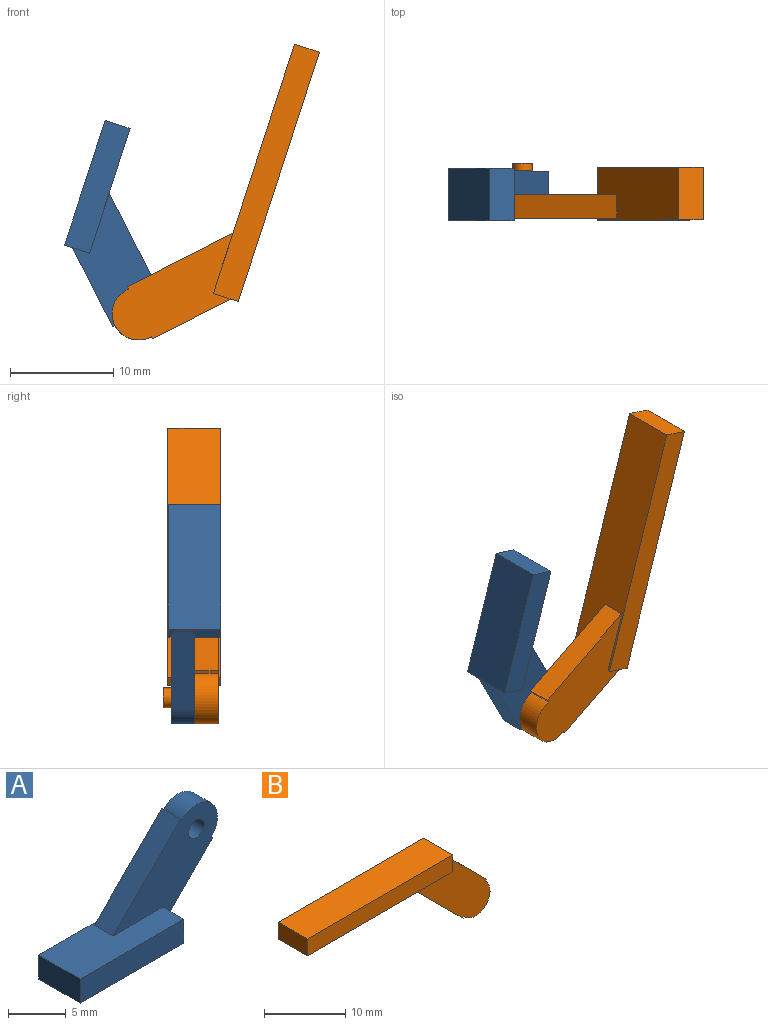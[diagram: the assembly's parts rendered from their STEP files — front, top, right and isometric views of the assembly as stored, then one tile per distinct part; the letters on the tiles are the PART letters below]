
ASSEMBLY  parts=2 mates=1
PART A: 15 faces, bbox 19.4x5.1x11.4 mm
  f0: plane 5.08x2.54mm, normal (1,0,0), area 8.9mm2, adj f1,f2,f4,f5,f7,f8,f9
  f1: plane 12.7x5.08mm, normal (0,0,1), area 50.6mm2, adj f0,f2,f3,f4,f8,f9,f14
  f2: plane 12.7x2.54mm, normal (0,1,0), area 32.3mm2, adj f0,f1,f3,f5
  f3: plane 5.08x2.54mm, normal (-1,0,0), area 12.9mm2, adj f1,f2,f4,f5
  f4: plane 12.7x2.54mm, normal (0,-1,0), area 32.3mm2, adj f0,f1,f3,f5
  f5: plane 12.7x5.08mm, normal (0,0,-1), area 64.5mm2, adj f0,f2,f3,f4
  f6: plane 8.27x8.27mm, normal (-0.71,0,0.71), area 26.7mm2, adj f8,f9,f10,f14
  f7: plane 6.09x6.09mm, normal (0.71,0,-0.71), area 19.7mm2, adj f0,f8,f9,f11
  f8: plane 12.78x10.6mm, normal (0,-1,0), area 58.5mm2, adj f0,f1,f6,f7,f10,f11,f12,f13
  f9: plane 12.78x10.6mm, normal (0,1,0), area 58.5mm2, adj f0,f1,f6,f7,f10,f11,f12,f13
  f10: plane 2.29x0.18mm, normal (0.71,0,0.71), area 0.6mm2, adj f6,f8,f9,f12
  f11: plane 2.29x0.18mm, normal (0.71,0,0.71), area 0.6mm2, adj f7,f8,f9,f12
  f12: cylinder r=2.54mm len=4.34mm, axis (0,1,0), area 18.2mm2, adj f8,f9,f10,f11
  f13: cylinder r=0.98mm len=2.29mm, axis (0,1,0), area 14mm2, adj f8,f9
  f14: plane 2.29x0.02mm, normal (-0.71,0,-0.71), area 0.1mm2, adj f1,f6,f8,f9
PART B: 16 faces, bbox 32.1x5.5x11.4 mm
  f0: plane 5.08x2.54mm, normal (1,0,0), area 8.9mm2, adj f1,f2,f4,f5,f8,f9,f10
  f1: plane 25.4x5.08mm, normal (0,0,-1), area 115.1mm2, adj f0,f2,f3,f4,f6,f9,f10
  f2: plane 25.4x2.54mm, normal (0,1,0), area 64.5mm2, adj f0,f1,f3,f5
  f3: plane 5.08x2.54mm, normal (-1,0,0), area 12.9mm2, adj f1,f2,f4,f5
  f4: plane 25.4x2.54mm, normal (0,-1,0), area 64.5mm2, adj f0,f1,f3,f5
  f5: plane 25.4x5.08mm, normal (0,0,1), area 129mm2, adj f0,f2,f3,f4
  f6: plane 2.29x0.02mm, normal (-0.71,0,0.71), area 0.1mm2, adj f1,f7,f9,f10
  f7: plane 8.08x8.08mm, normal (-0.71,0,-0.71), area 26.1mm2, adj f6,f9,f10,f12
  f8: plane 6.02x6.02mm, normal (0.71,0,0.71), area 19.5mm2, adj f0,f9,f10,f11
  f9: plane 12.78x10.6mm, normal (0,1,0), area 58.6mm2, adj f0,f1,f6,f7,f8,f11,f12,f13
  f10: plane 12.78x10.6mm, normal (0,-1,0), area 61.4mm2, adj f0,f1,f6,f7,f8,f11,f12,f13
  f11: plane 2.29x0.18mm, normal (0.71,0,-0.71), area 0.6mm2, adj f8,f9,f10,f13
  f12: plane 2.29x0.19mm, normal (0.71,0,-0.71), area 0.6mm2, adj f7,f9,f10,f13
  f13: cylinder r=2.54mm len=4.51mm, axis (0,-1,0), area 19mm2, adj f9,f10,f11,f12
  f14: cylinder r=0.95mm len=3.05mm, axis (0,-1,0), area 18.2mm2, adj f9,f15
  f15: plane 1.91x1.91mm, normal (0,1,0), area 2.9mm2, adj f14
PLACE A rot(axis=(0,1,0),108deg) t=(-1.56,21.08,14.73)mm
PLACE B rot(axis=(0,1,0),108deg) t=(14.81,21.08,16.09)mm
MATE revolute B.f13 <-> A.f12  axis (0,-1,0) through (3.62,21.08,2.05)mm
